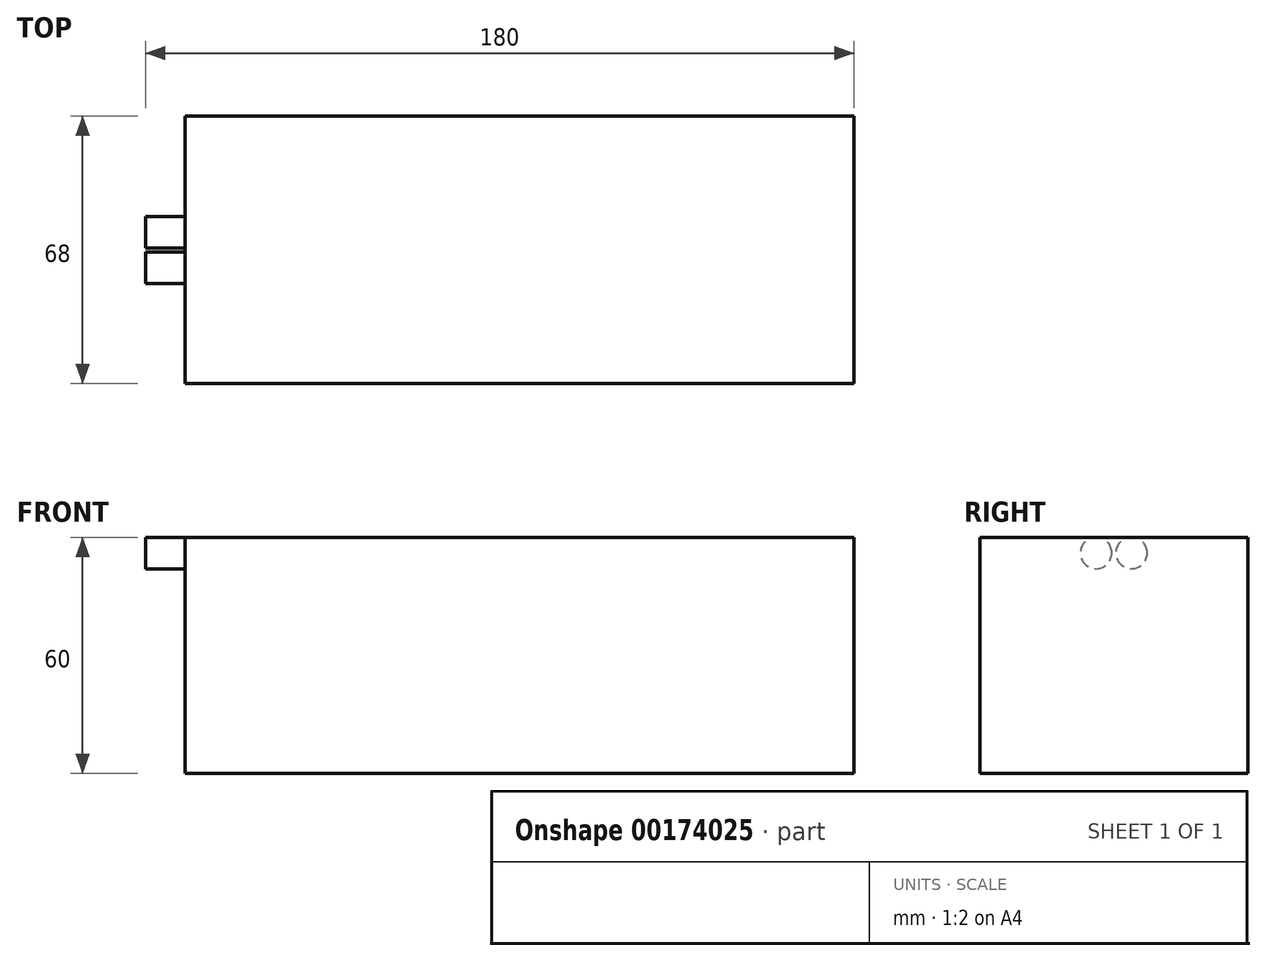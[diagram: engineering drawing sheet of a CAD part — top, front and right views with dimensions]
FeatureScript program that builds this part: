
annotation { "Feature Type Name" : "Feature", "Feature Type Description" : "" }
export const myFeature = defineFeature(function(context is Context, id is Id, definition is map)
    precondition{}
    {
        {
            var Q0;
            Q0=qCreatedBy(makeId("Top.planeOp"),FACE);
            var sketch = newSketch(context, id + "F0", { "sketchPlane" : qUnion([Q0])});
            skLineSegment(sketch, "E0.bottom", {"start": v(85, 34) * mm, "end": v(-85, 34) * mm});
            skLineSegment(sketch, "E0.top", {"start": v(85, -34) * mm, "end": v(-85, -34) * mm});
            skLineSegment(sketch, "E0.left", {"start": v(85, 34) * mm, "end": v(85, -34) * mm});
            skLineSegment(sketch, "E0.right", {"start": v(-85, 34) * mm, "end": v(-85, -34) * mm});
            skPoint(sketch, "E0.middle", {"position": v(0, 0) * mm});
            skSolve(sketch);
        }
        {
            var Q0;
            Q0 = qSketchRegion(id + "F0", true);
            extrude(context, id + "F1", {"entities" : qUnion([Q0]), "depth" : 60 * mm});
        }
        {
            var Q0;
            Q0=makeQuery(id+"F1.opExtrude","SWEPT_FACE",FACE,{"disambiguationData":[OSD([sQuery(id+"F0.wireOp",EDGE,"E0.right")])]});
            var sketch = newSketch(context, id + "F2", { "sketchPlane" : qUnion([Q0])});
            skLineSegment(sketch, "E1", {"start": v(0, 60) * mm, "end": v(0, 56) * mm, "construction": true});
            skPoint(sketch, "E1.endSnap0", {"position": v(0, 60) * mm});
            skCircle(sketch, "E2", {"center": v(4.5, 56) * mm, "radius": 4 * mm});
            skCircle(sketch, "E3", {"center": v(-4.5, 56) * mm, "radius": 4 * mm});
            skLineSegment(sketch, "E4", {"start": v(-4.5, 56) * mm, "end": v(4.5, 56) * mm, "construction": true});
            skSolve(sketch);
        }
        {
            var Q0;
            Q0 = qSketchRegion(id + "F2", true);
            extrude(context, id + "F3", {"entities" : qUnion([Q0]), "operationType" : NewBodyOperationType.ADD, "depth" : 10 * mm});
        }
    });
